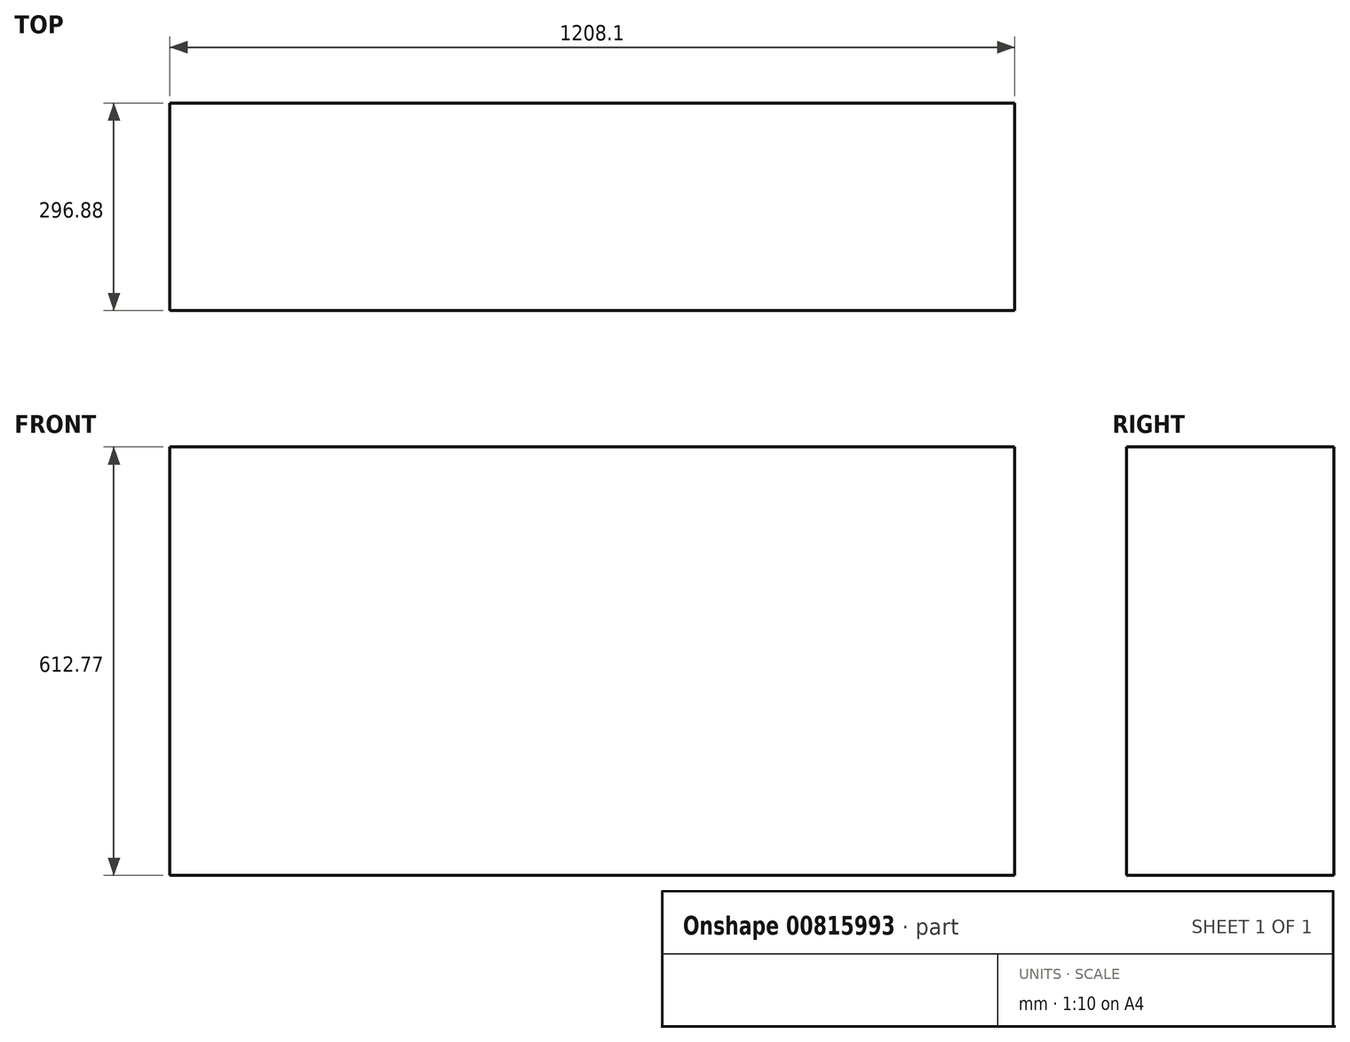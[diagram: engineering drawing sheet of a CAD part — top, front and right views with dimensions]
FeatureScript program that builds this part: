
annotation { "Feature Type Name" : "Feature", "Feature Type Description" : "" }
export const myFeature = defineFeature(function(context is Context, id is Id, definition is map)
    precondition{}
    {
        {
            var Q0;
            Q0=qCreatedBy(makeId("Top.planeOp"),FACE);
            var sketch = newSketch(context, id + "F0", { "sketchPlane" : qUnion([Q0])});
            skLineSegment(sketch, "E0.bottom", {"start": v(-604.05, 148.44) * mm, "end": v(604.05, 148.44) * mm});
            skLineSegment(sketch, "E0.top", {"start": v(-604.05, -148.44) * mm, "end": v(604.05, -148.44) * mm});
            skLineSegment(sketch, "E0.left", {"start": v(-604.05, 148.44) * mm, "end": v(-604.05, -148.44) * mm});
            skLineSegment(sketch, "E0.right", {"start": v(604.05, 148.44) * mm, "end": v(604.05, -148.44) * mm});
            skPoint(sketch, "E0.middle", {"position": v(0, 0) * mm});
            skSolve(sketch);
        }
        {
            var Q0;
            Q0 = qSketchRegion(id + "F0", true);
            extrude(context, id + "F1", {"entities" : qUnion([Q0]), "depth" : 612.77 * mm, "offsetDistance" : 25.4 * mm});
        }
    });
